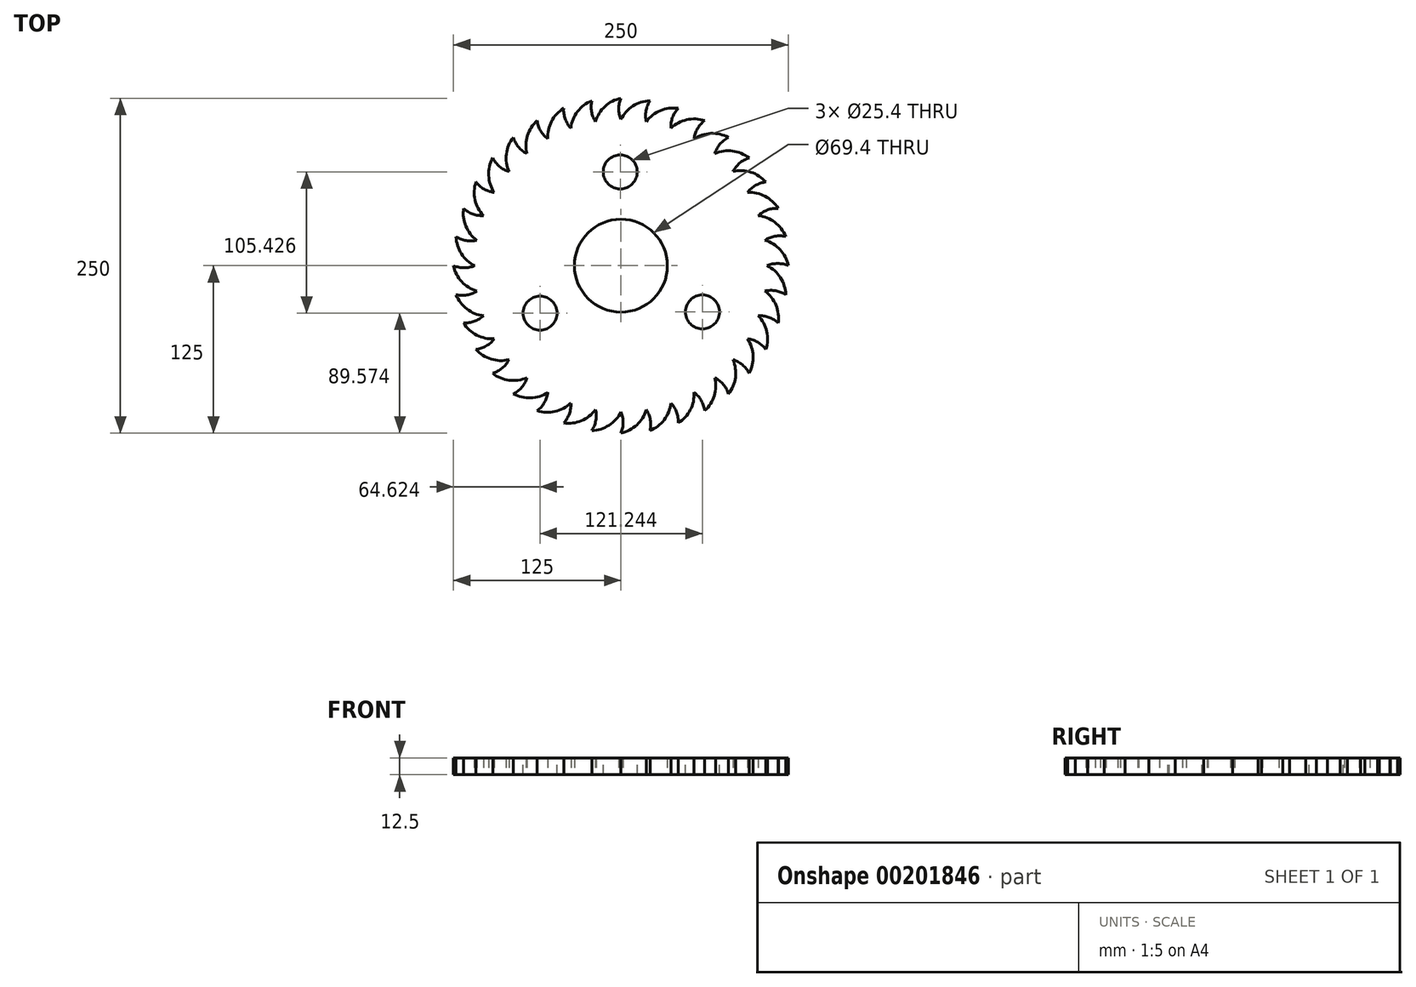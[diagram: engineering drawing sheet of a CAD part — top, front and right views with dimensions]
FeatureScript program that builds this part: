
annotation { "Feature Type Name" : "Feature", "Feature Type Description" : "" }
export const myFeature = defineFeature(function(context is Context, id is Id, definition is map)
    precondition{}
    {
        {
            var Q0;
            Q0=qCreatedBy(makeId("Top.planeOp"),FACE);
            var sketch = newSketch(context, id + "F0", { "sketchPlane" : qUnion([Q0])});
            skPoint(sketch, "E0.center", {"position": v(0, 0) * mm});
            skCircle(sketch, "E1", {"center": v(0, 0) * mm, "radius": 125 * mm, "construction": true});
            skCircle(sketch, "E2", {"center": v(0, 0) * mm, "radius": 109.2 * mm, "construction": true});
            skLineSegment(sketch, "E3", {"start": v(0, 0) * mm, "end": v(0, 178.7) * mm, "construction": true});
            skLineSegment(sketch, "E4", {"start": v(0, 0) * mm, "end": v(30.8, 174.64) * mm, "construction": true});
            skPoint(sketch, "E5", {"position": v(0, 109.2) * mm});
            skPoint(sketch, "E6", {"position": v(21.7, 123.1) * mm});
            skPoint(sketch, "E7", {"position": v(18.96, 107.54) * mm});
            skArc(sketch, "E8", {"start": v(21.7, 123.1) * mm, "mid": v(8.92, 119.16) * mm, "end": v(0, 109.2) * mm});
            skArc(sketch, "E9", {"start": v(21.7, 123.1) * mm, "mid": v(18.73, 115.6) * mm, "end": v(18.96, 107.54) * mm});
            skArc(sketch, "E10.1.0", {"start": v(0, 125) * mm, "mid": v(-11.9, 118.9) * mm, "end": v(-18.96, 107.54) * mm});
            skArc(sketch, "E10.1.1", {"start": v(0, 125) * mm, "mid": v(-1.63, 117.1) * mm, "end": v(0, 109.2) * mm});
            skArc(sketch, "E10.2.0", {"start": v(-21.7, 123.1) * mm, "mid": v(-32.37, 115.03) * mm, "end": v(-37.35, 102.61) * mm});
            skArc(sketch, "E10.2.1", {"start": v(-21.7, 123.1) * mm, "mid": v(-21.94, 115.04) * mm, "end": v(-18.96, 107.54) * mm});
            skArc(sketch, "E10.3.0", {"start": v(-42.75, 117.46) * mm, "mid": v(-51.85, 107.66) * mm, "end": v(-54.6, 94.57) * mm});
            skArc(sketch, "E10.3.1", {"start": v(-42.75, 117.46) * mm, "mid": v(-41.58, 109.48) * mm, "end": v(-37.35, 102.61) * mm});
            skArc(sketch, "E10.4.0", {"start": v(-62.5, 108.25) * mm, "mid": v(-69.76, 97.02) * mm, "end": v(-70.2, 83.65) * mm});
            skArc(sketch, "E10.4.1", {"start": v(-62.5, 108.25) * mm, "mid": v(-59.96, 100.6) * mm, "end": v(-54.6, 94.57) * mm});
            skArc(sketch, "E10.5.0", {"start": v(-80.35, 95.76) * mm, "mid": v(-85.55, 83.43) * mm, "end": v(-83.65, 70.2) * mm});
            skArc(sketch, "E10.5.1", {"start": v(-80.35, 95.76) * mm, "mid": v(-76.52, 88.66) * mm, "end": v(-70.2, 83.65) * mm});
            skArc(sketch, "E10.6.0", {"start": v(-95.76, 80.35) * mm, "mid": v(-98.74, 67.3) * mm, "end": v(-94.57, 54.6) * mm});
            skArc(sketch, "E10.6.1", {"start": v(-95.76, 80.35) * mm, "mid": v(-90.75, 74.02) * mm, "end": v(-83.65, 70.2) * mm});
            skArc(sketch, "E10.7.0", {"start": v(-108.25, 62.5) * mm, "mid": v(-108.93, 49.14) * mm, "end": v(-102.61, 37.35) * mm});
            skArc(sketch, "E10.7.1", {"start": v(-108.25, 62.5) * mm, "mid": v(-102.22, 57.14) * mm, "end": v(-94.57, 54.6) * mm});
            skArc(sketch, "E10.8.0", {"start": v(-117.46, 42.75) * mm, "mid": v(-115.8, 29.48) * mm, "end": v(-107.54, 18.96) * mm});
            skArc(sketch, "E10.8.1", {"start": v(-117.46, 42.75) * mm, "mid": v(-110.6, 38.52) * mm, "end": v(-102.61, 37.35) * mm});
            skArc(sketch, "E10.9.0", {"start": v(-123.1, 21.7) * mm, "mid": v(-119.16, 8.92) * mm, "end": v(-109.2, 0) * mm});
            skArc(sketch, "E10.9.1", {"start": v(-123.1, 21.7) * mm, "mid": v(-115.6, 18.73) * mm, "end": v(-107.54, 18.96) * mm});
            skArc(sketch, "E10.10.0", {"start": v(-125, 0) * mm, "mid": v(-118.9, -11.9) * mm, "end": v(-107.54, -18.96) * mm});
            skArc(sketch, "E10.10.1", {"start": v(-125, 0) * mm, "mid": v(-117.1, -1.63) * mm, "end": v(-109.2, 0) * mm});
            skArc(sketch, "E10.11.0", {"start": v(-123.1, -21.7) * mm, "mid": v(-115.03, -32.37) * mm, "end": v(-102.61, -37.35) * mm});
            skArc(sketch, "E10.11.1", {"start": v(-123.1, -21.7) * mm, "mid": v(-115.04, -21.94) * mm, "end": v(-107.54, -18.96) * mm});
            skArc(sketch, "E10.12.0", {"start": v(-117.46, -42.75) * mm, "mid": v(-107.66, -51.85) * mm, "end": v(-94.57, -54.6) * mm});
            skArc(sketch, "E10.12.1", {"start": v(-117.46, -42.75) * mm, "mid": v(-109.48, -41.58) * mm, "end": v(-102.61, -37.35) * mm});
            skArc(sketch, "E10.13.0", {"start": v(-108.25, -62.5) * mm, "mid": v(-97.02, -69.76) * mm, "end": v(-83.65, -70.2) * mm});
            skArc(sketch, "E10.13.1", {"start": v(-108.25, -62.5) * mm, "mid": v(-100.6, -59.96) * mm, "end": v(-94.57, -54.6) * mm});
            skArc(sketch, "E10.14.0", {"start": v(-95.76, -80.35) * mm, "mid": v(-83.43, -85.55) * mm, "end": v(-70.2, -83.65) * mm});
            skArc(sketch, "E10.14.1", {"start": v(-95.76, -80.35) * mm, "mid": v(-88.66, -76.52) * mm, "end": v(-83.65, -70.2) * mm});
            skArc(sketch, "E10.15.0", {"start": v(-80.35, -95.76) * mm, "mid": v(-67.3, -98.74) * mm, "end": v(-54.6, -94.57) * mm});
            skArc(sketch, "E10.15.1", {"start": v(-80.35, -95.76) * mm, "mid": v(-74.02, -90.75) * mm, "end": v(-70.2, -83.65) * mm});
            skArc(sketch, "E10.16.0", {"start": v(-62.5, -108.25) * mm, "mid": v(-49.14, -108.93) * mm, "end": v(-37.35, -102.61) * mm});
            skArc(sketch, "E10.16.1", {"start": v(-62.5, -108.25) * mm, "mid": v(-57.14, -102.22) * mm, "end": v(-54.6, -94.57) * mm});
            skArc(sketch, "E10.17.0", {"start": v(-42.75, -117.46) * mm, "mid": v(-29.48, -115.8) * mm, "end": v(-18.96, -107.54) * mm});
            skArc(sketch, "E10.17.1", {"start": v(-42.75, -117.46) * mm, "mid": v(-38.52, -110.6) * mm, "end": v(-37.35, -102.61) * mm});
            skArc(sketch, "E10.18.0", {"start": v(-21.7, -123.1) * mm, "mid": v(-8.92, -119.16) * mm, "end": v(0, -109.2) * mm});
            skArc(sketch, "E10.18.1", {"start": v(-21.7, -123.1) * mm, "mid": v(-18.73, -115.6) * mm, "end": v(-18.96, -107.54) * mm});
            skArc(sketch, "E10.19.0", {"start": v(0, -125) * mm, "mid": v(11.9, -118.9) * mm, "end": v(18.96, -107.54) * mm});
            skArc(sketch, "E10.19.1", {"start": v(0, -125) * mm, "mid": v(1.63, -117.1) * mm, "end": v(0, -109.2) * mm});
            skArc(sketch, "E10.20.0", {"start": v(21.7, -123.1) * mm, "mid": v(32.37, -115.03) * mm, "end": v(37.35, -102.61) * mm});
            skArc(sketch, "E10.20.1", {"start": v(21.7, -123.1) * mm, "mid": v(21.94, -115.04) * mm, "end": v(18.96, -107.54) * mm});
            skArc(sketch, "E10.21.0", {"start": v(42.75, -117.46) * mm, "mid": v(51.85, -107.66) * mm, "end": v(54.6, -94.57) * mm});
            skArc(sketch, "E10.21.1", {"start": v(42.75, -117.46) * mm, "mid": v(41.58, -109.48) * mm, "end": v(37.35, -102.61) * mm});
            skArc(sketch, "E10.22.0", {"start": v(62.5, -108.25) * mm, "mid": v(69.76, -97.02) * mm, "end": v(70.2, -83.65) * mm});
            skArc(sketch, "E10.22.1", {"start": v(62.5, -108.25) * mm, "mid": v(59.96, -100.6) * mm, "end": v(54.6, -94.57) * mm});
            skArc(sketch, "E10.23.0", {"start": v(80.35, -95.76) * mm, "mid": v(85.55, -83.43) * mm, "end": v(83.65, -70.2) * mm});
            skArc(sketch, "E10.23.1", {"start": v(80.35, -95.76) * mm, "mid": v(76.52, -88.66) * mm, "end": v(70.2, -83.65) * mm});
            skArc(sketch, "E10.24.0", {"start": v(95.76, -80.35) * mm, "mid": v(98.74, -67.3) * mm, "end": v(94.57, -54.6) * mm});
            skArc(sketch, "E10.24.1", {"start": v(95.76, -80.35) * mm, "mid": v(90.75, -74.02) * mm, "end": v(83.65, -70.2) * mm});
            skArc(sketch, "E10.25.0", {"start": v(108.25, -62.5) * mm, "mid": v(108.93, -49.14) * mm, "end": v(102.61, -37.35) * mm});
            skArc(sketch, "E10.25.1", {"start": v(108.25, -62.5) * mm, "mid": v(102.22, -57.14) * mm, "end": v(94.57, -54.6) * mm});
            skArc(sketch, "E10.26.0", {"start": v(117.46, -42.75) * mm, "mid": v(115.8, -29.48) * mm, "end": v(107.54, -18.96) * mm});
            skArc(sketch, "E10.26.1", {"start": v(117.46, -42.75) * mm, "mid": v(110.6, -38.52) * mm, "end": v(102.61, -37.35) * mm});
            skArc(sketch, "E10.27.0", {"start": v(123.1, -21.7) * mm, "mid": v(119.16, -8.92) * mm, "end": v(109.2, 0) * mm});
            skArc(sketch, "E10.27.1", {"start": v(123.1, -21.7) * mm, "mid": v(115.6, -18.73) * mm, "end": v(107.54, -18.96) * mm});
            skArc(sketch, "E10.28.0", {"start": v(125, 0) * mm, "mid": v(118.9, 11.9) * mm, "end": v(107.54, 18.96) * mm});
            skArc(sketch, "E10.28.1", {"start": v(125, 0) * mm, "mid": v(117.1, 1.63) * mm, "end": v(109.2, 0) * mm});
            skArc(sketch, "E10.29.0", {"start": v(123.1, 21.7) * mm, "mid": v(115.03, 32.37) * mm, "end": v(102.61, 37.35) * mm});
            skArc(sketch, "E10.29.1", {"start": v(123.1, 21.7) * mm, "mid": v(115.04, 21.94) * mm, "end": v(107.54, 18.96) * mm});
            skArc(sketch, "E10.30.0", {"start": v(117.46, 42.75) * mm, "mid": v(107.66, 51.85) * mm, "end": v(94.57, 54.6) * mm});
            skArc(sketch, "E10.30.1", {"start": v(117.46, 42.75) * mm, "mid": v(109.48, 41.58) * mm, "end": v(102.61, 37.35) * mm});
            skArc(sketch, "E10.31.0", {"start": v(108.25, 62.5) * mm, "mid": v(97.02, 69.76) * mm, "end": v(83.65, 70.2) * mm});
            skArc(sketch, "E10.31.1", {"start": v(108.25, 62.5) * mm, "mid": v(100.6, 59.96) * mm, "end": v(94.57, 54.6) * mm});
            skArc(sketch, "E10.32.0", {"start": v(95.76, 80.35) * mm, "mid": v(83.43, 85.55) * mm, "end": v(70.2, 83.65) * mm});
            skArc(sketch, "E10.32.1", {"start": v(95.76, 80.35) * mm, "mid": v(88.66, 76.52) * mm, "end": v(83.65, 70.2) * mm});
            skArc(sketch, "E10.33.0", {"start": v(80.35, 95.76) * mm, "mid": v(67.3, 98.74) * mm, "end": v(54.6, 94.57) * mm});
            skArc(sketch, "E10.33.1", {"start": v(80.35, 95.76) * mm, "mid": v(74.02, 90.75) * mm, "end": v(70.2, 83.65) * mm});
            skArc(sketch, "E10.34.0", {"start": v(62.5, 108.25) * mm, "mid": v(49.14, 108.93) * mm, "end": v(37.35, 102.61) * mm});
            skArc(sketch, "E10.34.1", {"start": v(62.5, 108.25) * mm, "mid": v(57.14, 102.22) * mm, "end": v(54.6, 94.57) * mm});
            skArc(sketch, "E10.35.0", {"start": v(42.75, 117.46) * mm, "mid": v(29.48, 115.8) * mm, "end": v(18.96, 107.54) * mm});
            skArc(sketch, "E10.35.1", {"start": v(42.75, 117.46) * mm, "mid": v(38.52, 110.6) * mm, "end": v(37.35, 102.61) * mm});
            skCircle(sketch, "E11", {"center": v(0, 0) * mm, "radius": 34.7 * mm});
            skSolve(sketch);
        }
        {
            var Q0;
            Q0=makeQuery(id+"F0.imprint","IMPRINT",FACE,{"disambiguationData":[TD([[makeQuery(id+"F0.imprint","IMPRINT",EDGE,{"derivedFrom":sQuery(id+"F0.wireOp",EDGE,"E8")}),1.0]])]});
            extrude(context, id + "F1", {"entities" : qUnion([Q0]), "depth" : 12.5 * mm});
        }
        {
            var Q0;
            Q0=makeQuery(id+"F1.opExtrude","CAP_FACE",FACE,{"disambiguationData":[OSD([sQuery(id+"F0.wireOp",EDGE,"E8"),sQuery(id+"F0.wireOp",EDGE,"E9"),sQuery(id+"F0.wireOp",EDGE,"E10.1.0"),sQuery(id+"F0.wireOp",EDGE,"E10.1.1"),sQuery(id+"F0.wireOp",EDGE,"E10.2.0"),sQuery(id+"F0.wireOp",EDGE,"E10.2.1"),sQuery(id+"F0.wireOp",EDGE,"E10.3.0"),sQuery(id+"F0.wireOp",EDGE,"E10.3.1"),sQuery(id+"F0.wireOp",EDGE,"E10.4.0"),sQuery(id+"F0.wireOp",EDGE,"E10.4.1"),sQuery(id+"F0.wireOp",EDGE,"E10.5.0"),sQuery(id+"F0.wireOp",EDGE,"E10.5.1"),sQuery(id+"F0.wireOp",EDGE,"E10.6.0"),sQuery(id+"F0.wireOp",EDGE,"E10.6.1"),sQuery(id+"F0.wireOp",EDGE,"E10.7.0"),sQuery(id+"F0.wireOp",EDGE,"E10.7.1"),sQuery(id+"F0.wireOp",EDGE,"E10.8.0"),sQuery(id+"F0.wireOp",EDGE,"E10.8.1"),sQuery(id+"F0.wireOp",EDGE,"E10.9.0"),sQuery(id+"F0.wireOp",EDGE,"E10.9.1"),sQuery(id+"F0.wireOp",EDGE,"E10.10.0"),sQuery(id+"F0.wireOp",EDGE,"E10.10.1"),sQuery(id+"F0.wireOp",EDGE,"E10.11.0"),sQuery(id+"F0.wireOp",EDGE,"E10.11.1"),sQuery(id+"F0.wireOp",EDGE,"E10.12.0"),sQuery(id+"F0.wireOp",EDGE,"E10.12.1"),sQuery(id+"F0.wireOp",EDGE,"E10.13.0"),sQuery(id+"F0.wireOp",EDGE,"E10.13.1"),sQuery(id+"F0.wireOp",EDGE,"E10.14.0"),sQuery(id+"F0.wireOp",EDGE,"E10.14.1"),sQuery(id+"F0.wireOp",EDGE,"E10.15.0"),sQuery(id+"F0.wireOp",EDGE,"E10.15.1"),sQuery(id+"F0.wireOp",EDGE,"E10.16.0"),sQuery(id+"F0.wireOp",EDGE,"E10.16.1"),sQuery(id+"F0.wireOp",EDGE,"E10.17.0"),sQuery(id+"F0.wireOp",EDGE,"E10.17.1"),sQuery(id+"F0.wireOp",EDGE,"E10.18.0"),sQuery(id+"F0.wireOp",EDGE,"E10.18.1"),sQuery(id+"F0.wireOp",EDGE,"E10.19.0"),sQuery(id+"F0.wireOp",EDGE,"E10.19.1"),sQuery(id+"F0.wireOp",EDGE,"E10.20.0"),sQuery(id+"F0.wireOp",EDGE,"E10.20.1"),sQuery(id+"F0.wireOp",EDGE,"E10.21.0"),sQuery(id+"F0.wireOp",EDGE,"E10.21.1"),sQuery(id+"F0.wireOp",EDGE,"E10.22.0"),sQuery(id+"F0.wireOp",EDGE,"E10.22.1"),sQuery(id+"F0.wireOp",EDGE,"E10.23.0"),sQuery(id+"F0.wireOp",EDGE,"E10.23.1"),sQuery(id+"F0.wireOp",EDGE,"E10.24.0"),sQuery(id+"F0.wireOp",EDGE,"E10.24.1"),sQuery(id+"F0.wireOp",EDGE,"E10.25.0"),sQuery(id+"F0.wireOp",EDGE,"E10.25.1"),sQuery(id+"F0.wireOp",EDGE,"E10.26.0"),sQuery(id+"F0.wireOp",EDGE,"E10.26.1"),sQuery(id+"F0.wireOp",EDGE,"E10.27.0"),sQuery(id+"F0.wireOp",EDGE,"E10.27.1"),sQuery(id+"F0.wireOp",EDGE,"E10.28.0"),sQuery(id+"F0.wireOp",EDGE,"E10.28.1"),sQuery(id+"F0.wireOp",EDGE,"E10.29.0"),sQuery(id+"F0.wireOp",EDGE,"E10.29.1"),sQuery(id+"F0.wireOp",EDGE,"E10.30.0"),sQuery(id+"F0.wireOp",EDGE,"E10.30.1"),sQuery(id+"F0.wireOp",EDGE,"E10.31.0"),sQuery(id+"F0.wireOp",EDGE,"E10.31.1"),sQuery(id+"F0.wireOp",EDGE,"E10.32.0"),sQuery(id+"F0.wireOp",EDGE,"E10.32.1"),sQuery(id+"F0.wireOp",EDGE,"E10.33.0"),sQuery(id+"F0.wireOp",EDGE,"E10.33.1"),sQuery(id+"F0.wireOp",EDGE,"E10.34.0"),sQuery(id+"F0.wireOp",EDGE,"E10.34.1"),sQuery(id+"F0.wireOp",EDGE,"E10.35.0"),sQuery(id+"F0.wireOp",EDGE,"E10.35.1"),sQuery(id+"F0.wireOp",EDGE,"E11")])],"isStart":false});
            var sketch = newSketch(context, id + "F2", { "sketchPlane" : qUnion([Q0])});
            skCircle(sketch, "E12", {"center": v(-0.5, 70) * mm, "radius": 12.7 * mm});
            skCircle(sketch, "E13.1.0", {"center": v(-60.38, -35.43) * mm, "radius": 12.7 * mm});
            skCircle(sketch, "E13.2.0", {"center": v(60.87, -34.57) * mm, "radius": 12.7 * mm});
            skPoint(sketch, "E13.center", {"position": v(0, 0) * mm});
            skSolve(sketch);
        }
        {
            var Q0;
            Q0 = qSketchRegion(id + "F2", true);
            extrude(context, id + "F3", {"entities" : qUnion([Q0]), "operationType" : NewBodyOperationType.REMOVE, "oppositeDirection" : true, "depth" : 25 * mm});
        }
    });
